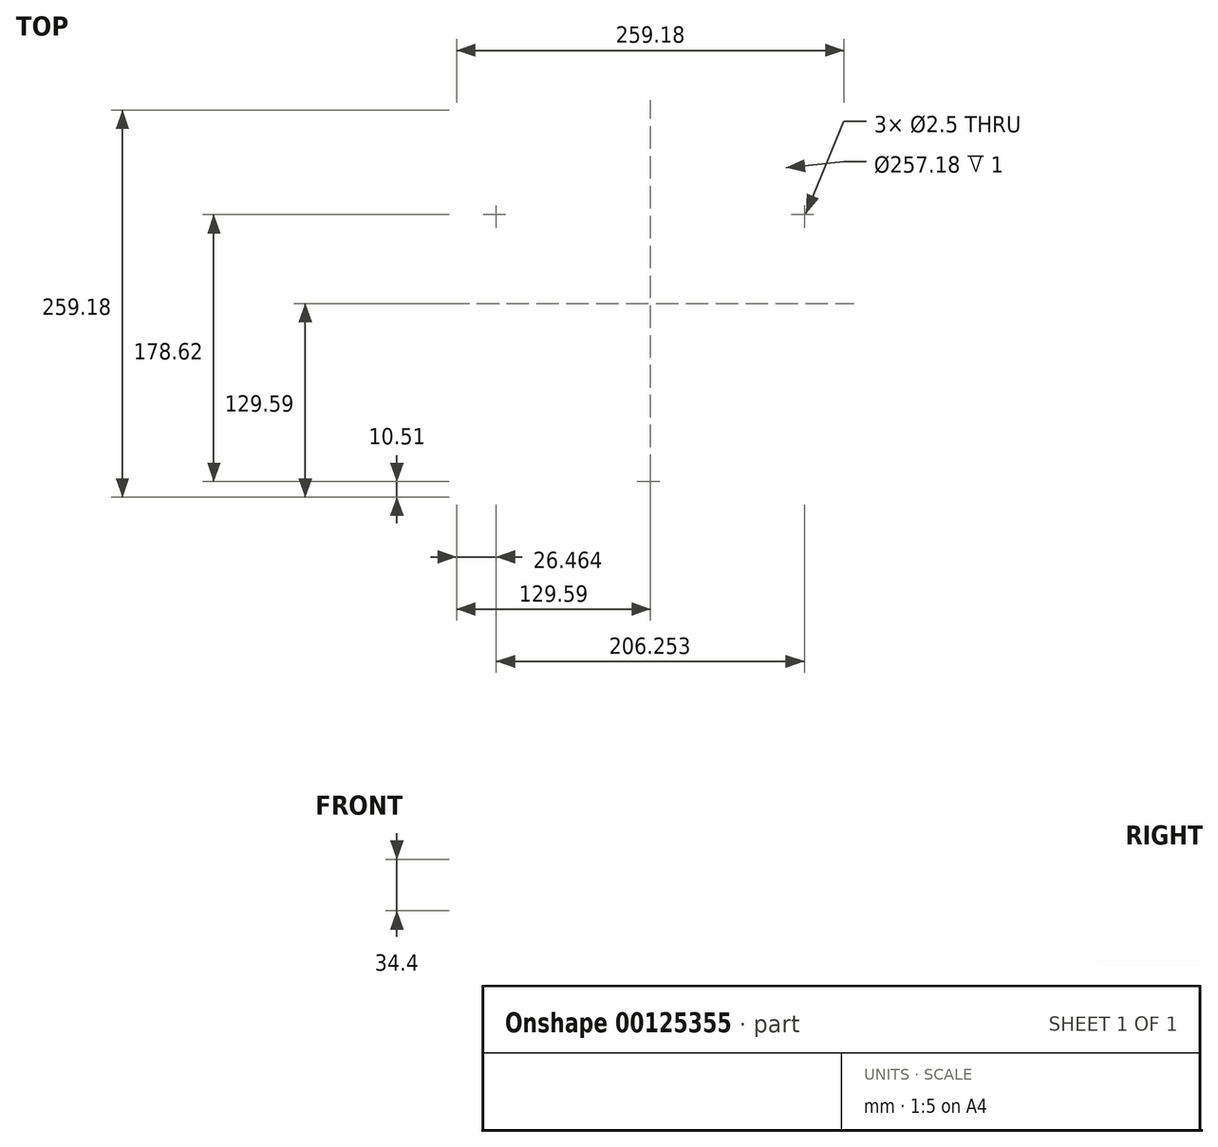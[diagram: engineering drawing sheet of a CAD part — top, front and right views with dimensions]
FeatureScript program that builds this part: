
annotation { "Feature Type Name" : "Feature", "Feature Type Description" : "" }
export const myFeature = defineFeature(function(context is Context, id is Id, definition is map)
    precondition{}
    {
        {
            var Q0;
            Q0=qCreatedBy(makeId("Top.planeOp"),FACE);
            var sketch = newSketch(context, id + "F0", { "sketchPlane" : qUnion([Q0])});
            skCircle(sketch, "E0", {"center": v(0, 0) * mm, "radius": 128.59 * mm});
            skSolve(sketch);
        }
        {
            var Q0;
            Q0=makeQuery(id+"F0.imprint","IMPRINT",FACE,{"disambiguationData":[TD([[makeQuery(id+"F0.imprint","IMPRINT",EDGE,{"derivedFrom":sQuery(id+"F0.wireOp",EDGE,"E0")}),1.0]])]});
            extrude(context, id + "F1", {"entities" : qUnion([Q0]), "depth" : 27.94 * mm});
        }
        {
            var Q0;
            Q0=qCreatedBy(makeId("Right.planeOp"),FACE);
            var sketch = newSketch(context, id + "F2", { "sketchPlane" : qUnion([Q0])});
            skLineSegment(sketch, "E1.0", {"start": v(-128.59, 27.94) * mm, "end": v(128.59, 27.94) * mm, "construction": true});
            skLineSegment(sketch, "E2", {"start": v(-60.13, 0) * mm, "end": v(56.7, 0) * mm, "construction": true});
            skLineSegment(sketch, "E3", {"start": v(56.7, 0) * mm, "end": v(128.59, 0) * mm});
            skLineSegment(sketch, "E4", {"start": v(128.59, 0) * mm, "end": v(128.59, 26.94) * mm});
            skLineSegment(sketch, "E5", {"start": v(128.59, 26.94) * mm, "end": v(91.62, 26.94) * mm});
            skLineSegment(sketch, "E6", {"start": v(56.7, 0) * mm, "end": v(56.7, 1) * mm});
            skLineSegment(sketch, "E7", {"start": v(56.7, 1) * mm, "end": v(91.62, 26.94) * mm});
            skSolve(sketch);
        }
        {
            var Q0;
            Q0 = qSketchRegion(id + "F2", true);
            var Q1;
            Q1=makeQuery(id+"F1.opExtrude","SWEPT_FACE",FACE,{"disambiguationData":[OSD([sQuery(id+"F0.wireOp",EDGE,"E0")])]});
            revolve(context, id + "F3", {"operationType" : NewBodyOperationType.REMOVE, "entities" : qUnion([Q0]), "axis" : qUnion([Q1]), "revolveType" : RevolveType.FULL, "oppositeDirection" : true});
        }
        {
            var Q0;
            Q0=makeQuery(id+"F1.opExtrude","CAP_FACE",FACE,{"disambiguationData":[OSD([sQuery(id+"F0.wireOp",EDGE,"E0"),sQuery(id+"F0.wireOp",EDGE,"UCFLERy4-zCuP-WeA9-FjO4-VpVRq7PdscQR")])],"isStart":false});
            shell(context, id + "F4", {"entities" : qUnion([Q0]), "thickness" : 1 * mm, "oppositeDirection" : true});
        }
        {
            var Q0;
            Q0=sQuery(id+"F0.wireOp",VERTEX,"E0.center");
            var Q1;
            Q1=makeQuery(id+"F1.opExtrude","SWEPT_BODY",BODY,{"disambiguationData":[OSD([sQuery(id+"F0.wireOp",EDGE,"E0")])]});
            hole(context, id + "F5", {"style" : HoleStyle.SIMPLE, "endStyle" : HoleEndStyle.THROUGH, "holeDiameter" : 116.84 * mm, "locations" : qUnion([Q0]), "scope" : qUnion([Q1]), "isTappedThrough" : true});
        }
        {
            var Q0;
            Q0=qCreatedBy(makeId("Right.planeOp"),FACE);
            var sketch = newSketch(context, id + "F6", { "sketchPlane" : qUnion([Q0])});
            skLineSegment(sketch, "E8.0", {"start": v(56.7, 1) * mm, "end": v(91.62, 26.94) * mm});
            skLineSegment(sketch, "E9", {"start": v(56.7, 1) * mm, "end": v(56.7, 20.6) * mm});
            skLineSegment(sketch, "E10", {"start": v(56.7, 20.6) * mm, "end": v(75.28, 34.4) * mm});
            skLineSegment(sketch, "E11", {"start": v(75.28, 34.4) * mm, "end": v(90.25, 25.92) * mm});
            skLineSegment(sketch, "E12", {"start": v(90.25, 25.92) * mm, "end": v(56.7, 1) * mm});
            skSolve(sketch);
        }
        {
            var Q0;
            Q0=makeQuery(id+"F6.imprint","IMPRINT",FACE,{"disambiguationData":[TD([[makeQuery(id+"F6.imprint","IMPRINT",EDGE,{"derivedFrom":sQuery(id+"F6.wireOp",EDGE,"E9")}),-1.0]])]});
            extrude(context, id + "F7", {"entities" : qUnion([Q0]), "operationType" : NewBodyOperationType.ADD, "endBound" : BoundingType.SYMMETRIC, "depth" : 15.25 * mm});
        }
        {
            var Q0;
            Q0=makeQuery(id+"F1.opExtrude","SWEPT_BODY",BODY,{"disambiguationData":[OSD([sQuery(id+"F0.wireOp",EDGE,"E0")])]});
            var Q1;
            Q1=makeQuery(id+"F4.opShell","OFFSET_EDGE",EDGE,{"disambiguationData":[OSD([sQuery(id+"F2.wireOp",EDGE,"E6"),sQuery(id+"F2.wireOp",EDGE,"E7")])]});
            circularPattern(context, id + "F8", {"operationType" : NewBodyOperationType.ADD, "entities" : qUnion([Q0]), "axis" : qUnion([Q1]), "angle" : 120 * degree, "instanceCount" : 3});
        }
        {
            var Q0;
            Q0=qCreatedBy(makeId("Top.planeOp"),FACE);
            var sketch = newSketch(context, id + "F9", { "sketchPlane" : qUnion([Q0])});
            skPoint(sketch, "E13.center", {"position": v(0, 0) * mm});
            skLineSegment(sketch, "E14", {"start": v(0, 0) * mm, "end": v(-103.13, 59.54) * mm, "construction": true});
            skCircle(sketch, "E15", {"center": v(-103.13, 59.54) * mm, "radius": 1.25 * mm});
            skCircle(sketch, "E16.1.0", {"center": v(0, -119.08) * mm, "radius": 1.25 * mm});
            skCircle(sketch, "E16.2.0", {"center": v(103.13, 59.54) * mm, "radius": 1.25 * mm});
            skSolve(sketch);
        }
        {
            var Q0;
            Q0 = qSketchRegion(id + "F9", true);
            extrude(context, id + "F10", {"entities" : qUnion([Q0]), "operationType" : NewBodyOperationType.REMOVE, "endBound" : BoundingType.THROUGH_ALL, "depth" : 25 * mm});
        }
    });
